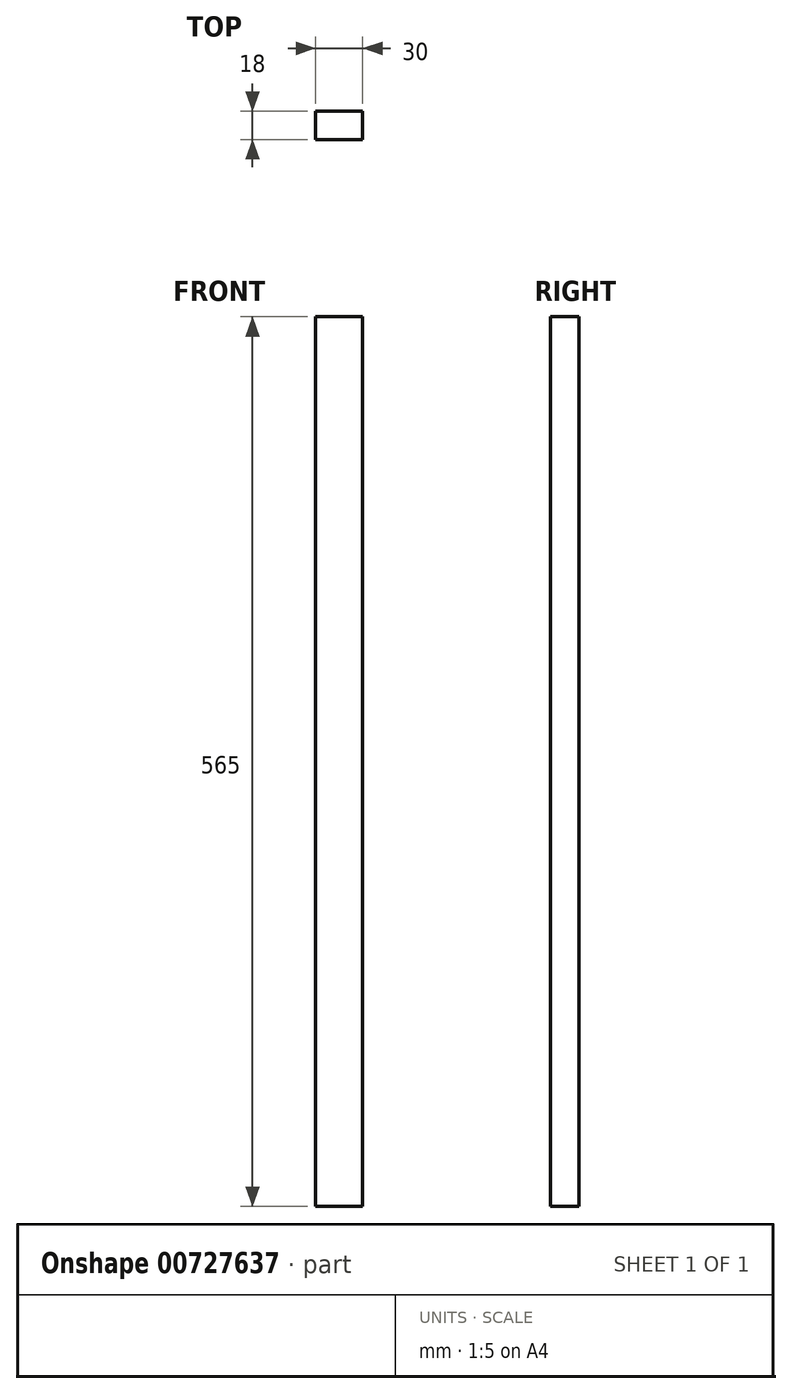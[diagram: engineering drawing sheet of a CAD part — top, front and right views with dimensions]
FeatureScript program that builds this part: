
annotation { "Feature Type Name" : "Feature", "Feature Type Description" : "" }
export const myFeature = defineFeature(function(context is Context, id is Id, definition is map)
    precondition{}
    {
        {
            var Q0;
            Q0=qCreatedBy(makeId("Front.planeOp"),FACE);
            var sketch = newSketch(context, id + "F0", { "sketchPlane" : qUnion([Q0])});
            skLineSegment(sketch, "E0.bottom", {"start": v(-15, -282.5) * mm, "end": v(15, -282.5) * mm});
            skLineSegment(sketch, "E0.top", {"start": v(-15, 282.5) * mm, "end": v(15, 282.5) * mm});
            skLineSegment(sketch, "E0.left", {"start": v(-15, -282.5) * mm, "end": v(-15, 282.5) * mm});
            skLineSegment(sketch, "E0.right", {"start": v(15, -282.5) * mm, "end": v(15, 282.5) * mm});
            skPoint(sketch, "E0.middle", {"position": v(0, 0) * mm});
            skSolve(sketch);
        }
        {
            var Q0;
            Q0 = qSketchRegion(id + "F0", true);
            extrude(context, id + "F1", {"entities" : qUnion([Q0]), "oppositeDirection" : true, "depth" : 18 * mm, "offsetDistance" : 25 * mm});
        }
    });
